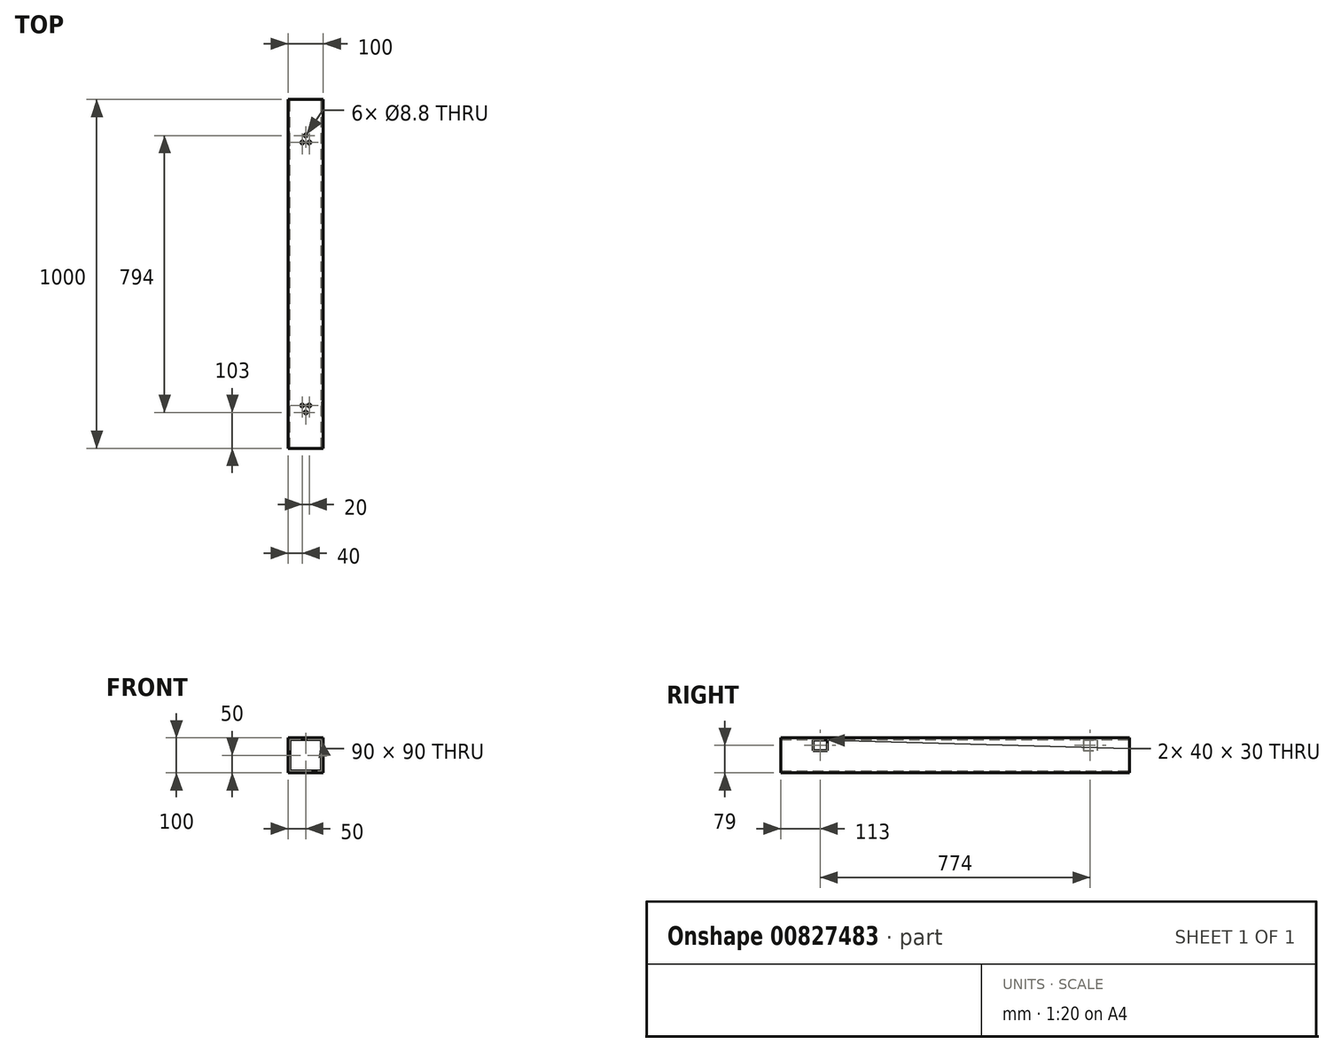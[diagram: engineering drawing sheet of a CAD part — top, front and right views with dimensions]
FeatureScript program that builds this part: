
annotation { "Feature Type Name" : "Feature", "Feature Type Description" : "" }
export const myFeature = defineFeature(function(context is Context, id is Id, definition is map)
    precondition{}
    {
        {
            var Q0;
            Q0=qCreatedBy(makeId("Front.planeOp"),FACE);
            var sketch = newSketch(context, id + "F0", { "sketchPlane" : qUnion([Q0])});
            skLineSegment(sketch, "E0.bottom", {"start": v(0, 0) * mm, "end": v(100, 0) * mm});
            skLineSegment(sketch, "E0.top", {"start": v(0, 100) * mm, "end": v(100, 100) * mm});
            skLineSegment(sketch, "E0.left", {"start": v(0, 0) * mm, "end": v(0, 100) * mm});
            skLineSegment(sketch, "E0.right", {"start": v(100, 0) * mm, "end": v(100, 100) * mm});
            skLineSegment(sketch, "E1.0", {"start": v(5, 95) * mm, "end": v(95, 95) * mm});
            skLineSegment(sketch, "E1.1", {"start": v(5, 5) * mm, "end": v(5, 95) * mm});
            skLineSegment(sketch, "E1.2", {"start": v(5, 5) * mm, "end": v(95, 5) * mm});
            skLineSegment(sketch, "E1.3", {"start": v(95, 5) * mm, "end": v(95, 95) * mm});
            skSolve(sketch);
        }
        {
            var Q0;
            Q0 = qSketchRegion(id + "F0", true);
            extrude(context, id + "F1", {"entities" : qUnion([Q0]), "depth" : 1000 * mm, "offsetDistance" : 25 * mm});
        }
        {
            var Q0;
            Q0=makeQuery(id+"F1.opExtrude","SWEPT_FACE",FACE,{"disambiguationData":[OSD([sQuery(id+"F0.wireOp",EDGE,"E0.right")])]});
            var sketch = newSketch(context, id + "F2", { "sketchPlane" : qUnion([Q0])});
            skLineSegment(sketch, "E2", {"start": v(-500, 175.93) * mm, "end": v(-500, -183.5) * mm, "construction": true});
            skPoint(sketch, "E2.startSnap0", {"position": v(-500, 100) * mm});
            skLineSegment(sketch, "E3", {"start": v(-1020.04, 50) * mm, "end": v(26.73, 50) * mm, "construction": true});
            skPoint(sketch, "E3.startSnap0", {"position": v(-1000, 50) * mm});
            skLineSegment(sketch, "E4", {"start": v(-857, 180.13) * mm, "end": v(-857, -129.9) * mm, "construction": true});
            skLineSegment(sketch, "E5", {"start": v(-143, 194.84) * mm, "end": v(-143, -148.83) * mm, "construction": true});
            skLineSegment(sketch, "E6.0", {"start": v(-875, 180.13) * mm, "end": v(-875, -129.9) * mm, "construction": true});
            skLineSegment(sketch, "E7.MirrorCS", {"start": v(-125, 180.13) * mm, "end": v(-125, -129.9) * mm, "construction": true});
            skLineSegment(sketch, "E8.bottom", {"start": v(-867, 94) * mm, "end": v(-907, 94) * mm});
            skLineSegment(sketch, "E8.top", {"start": v(-867, 64) * mm, "end": v(-907, 64) * mm});
            skLineSegment(sketch, "E8.left", {"start": v(-867, 94) * mm, "end": v(-867, 64) * mm});
            skLineSegment(sketch, "E8.right", {"start": v(-907, 94) * mm, "end": v(-907, 64) * mm});
            skSolve(sketch);
        }
        {
            var Q0;
            Q0 = qSketchRegion(id + "F2", true);
            extrude(context, id + "F3", {"entities" : qUnion([Q0]), "operationType" : NewBodyOperationType.REMOVE, "oppositeDirection" : true, "depth" : 5 * mm, "offsetDistance" : 25 * mm});
        }
        {
            var Q0;
            Q0=makeQuery(id+"F1.opExtrude","SWEPT_FACE",FACE,{"disambiguationData":[OSD([sQuery(id+"F0.wireOp",EDGE,"E0.left")])]});
            var sketch = newSketch(context, id + "F4", { "sketchPlane" : qUnion([Q0])});
            skLineSegment(sketch, "E9", {"start": v(500, 167.2) * mm, "end": v(500, -192.23) * mm, "construction": true});
            skPoint(sketch, "E9.startSnap0", {"position": v(500, 91.27) * mm});
            skLineSegment(sketch, "E10", {"start": v(-144.15, 41.27) * mm, "end": v(902.63, 41.27) * mm, "construction": true});
            skPoint(sketch, "E10.startSnap0", {"position": v(-124.1, 41.27) * mm});
            skLineSegment(sketch, "E11", {"start": v(143, 171.4) * mm, "end": v(143, -138.63) * mm, "construction": true});
            skLineSegment(sketch, "E12", {"start": v(857, 186.12) * mm, "end": v(857, -157.55) * mm, "construction": true});
            skLineSegment(sketch, "E13.0", {"start": v(125, 171.4) * mm, "end": v(125, -138.63) * mm, "construction": true});
            skLineSegment(sketch, "E14.MirrorCS", {"start": v(875, 171.4) * mm, "end": v(875, -138.63) * mm, "construction": true});
            skLineSegment(sketch, "E15.bottom", {"start": v(133, 94) * mm, "end": v(93, 94) * mm});
            skLineSegment(sketch, "E15.top", {"start": v(133, 64) * mm, "end": v(93, 64) * mm});
            skLineSegment(sketch, "E15.left", {"start": v(133, 94) * mm, "end": v(133, 64) * mm});
            skLineSegment(sketch, "E15.right", {"start": v(93, 94) * mm, "end": v(93, 64) * mm});
            skPoint(sketch, "E16", {"position": v(500, 100) * mm});
            skPoint(sketch, "E17", {"position": v(0, 50) * mm});
            skSolve(sketch);
        }
        {
            var Q0;
            Q0 = qSketchRegion(id + "F4", true);
            extrude(context, id + "F5", {"entities" : qUnion([Q0]), "operationType" : NewBodyOperationType.REMOVE, "oppositeDirection" : true, "depth" : 5 * mm, "offsetDistance" : 25 * mm});
        }
        {
            var Q0;
            Q0=makeQuery(id+"F1.opExtrude","SWEPT_FACE",FACE,{"disambiguationData":[OSD([sQuery(id+"F0.wireOp",EDGE,"E0.top")])]});
            var sketch = newSketch(context, id + "F6", { "sketchPlane" : qUnion([Q0])});
            skLineSegment(sketch, "E18", {"start": v(-180.77, -500) * mm, "end": v(283.8, -500) * mm, "construction": true});
            skPoint(sketch, "E18.startSnap0", {"position": v(0, -500) * mm});
            skLineSegment(sketch, "E19", {"start": v(50, 53.79) * mm, "end": v(50, -1016.9) * mm, "construction": true});
            skPoint(sketch, "E19.startSnap0", {"position": v(50, 0) * mm});
            skLineSegment(sketch, "E20", {"start": v(-186.21, -143) * mm, "end": v(281.98, -143) * mm, "construction": true});
            skLineSegment(sketch, "E21", {"start": v(-186.21, -857) * mm, "end": v(352.76, -857) * mm, "construction": true});
            skLineSegment(sketch, "E22.bottom", {"start": v(20, -143) * mm, "end": v(80, -143) * mm, "construction": true});
            skLineSegment(sketch, "E22.top", {"start": v(20, -83) * mm, "end": v(80, -83) * mm, "construction": true});
            skLineSegment(sketch, "E22.left", {"start": v(20, -143) * mm, "end": v(20, -83) * mm, "construction": true});
            skLineSegment(sketch, "E22.right", {"start": v(80, -143) * mm, "end": v(80, -83) * mm, "construction": true});
            skPoint(sketch, "E23.positionSnap0", {"position": v(20, -113) * mm});
            skPoint(sketch, "E24", {"position": v(50, -103) * mm});
            skPoint(sketch, "E25", {"position": v(40, -123) * mm});
            skPoint(sketch, "E26", {"position": v(60, -123) * mm});
            skPoint(sketch, "E27.MirrorP", {"position": v(40, -877) * mm});
            skPoint(sketch, "E28.MirrorP", {"position": v(50, -897) * mm});
            skPoint(sketch, "E29.MirrorP", {"position": v(60, -877) * mm});
            skSolve(sketch);
        }
        {
            var Q0;
            Q0=sQuery(id+"F6.wireOp",VERTEX,"E24");
            var Q1;
            Q1=sQuery(id+"F6.wireOp",VERTEX,"E25");
            var Q2;
            Q2=sQuery(id+"F6.wireOp",VERTEX,"E26");
            var Q3;
            Q3=sQuery(id+"F6.wireOp",VERTEX,"E27.MirrorP");
            var Q4;
            Q4=sQuery(id+"F6.wireOp",VERTEX,"E29.MirrorP");
            var Q5;
            Q5=sQuery(id+"F6.wireOp",VERTEX,"E28.MirrorP");
            var Q6;
            Q6=makeQuery(id+"F1.opExtrude","SWEPT_BODY",BODY,{"disambiguationData":[OSD([sQuery(id+"F0.wireOp",EDGE,"E0.bottom"),sQuery(id+"F0.wireOp",EDGE,"E0.top"),sQuery(id+"F0.wireOp",EDGE,"E0.left"),sQuery(id+"F0.wireOp",EDGE,"E0.right"),sQuery(id+"F0.wireOp",EDGE,"E1.0"),sQuery(id+"F0.wireOp",EDGE,"E1.1"),sQuery(id+"F0.wireOp",EDGE,"E1.2"),sQuery(id+"F0.wireOp",EDGE,"E1.3")])]});
            hole(context, id + "F7", {"style" : HoleStyle.SIMPLE, "endStyle" : HoleEndStyle.BLIND, "standardTappedOrClearance" : lookupTablePath({ "standard" : "ISO", "fit" : "Normal", "size" : "M8", "type" : "Clearance" }), "standardBlindInLast" : lookupTablePath({ "fit" : "Standard", "standard" : "ISO", "size" : "M8", "type" : "Clearance" }), "holeDiameter" : 8.8 * mm, "majorDiameter" : 8 * mm, "holeDepth" : 5 * mm, "isTappedThrough" : true, "tappedDepth" : 12 * mm, "tapClearance" : 3, "locations" : qUnion([Q0, Q1, Q2, Q3, Q4, Q5]), "scope" : qUnion([Q6])});
        }
    });
